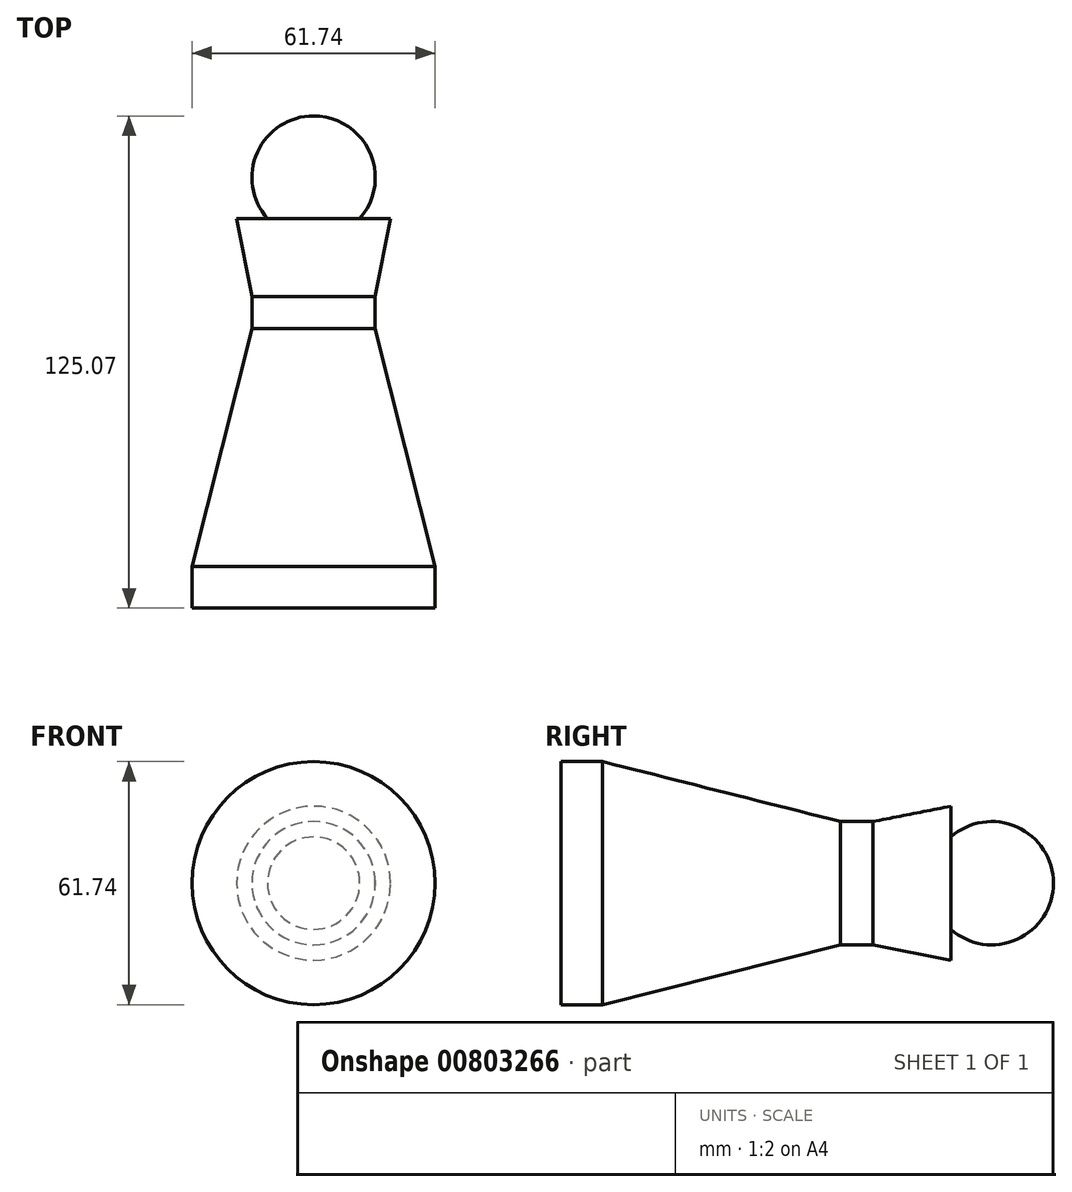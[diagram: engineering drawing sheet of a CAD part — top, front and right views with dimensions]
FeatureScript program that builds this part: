
annotation { "Feature Type Name" : "Feature", "Feature Type Description" : "" }
export const myFeature = defineFeature(function(context is Context, id is Id, definition is map)
    precondition{}
    {
        {
            var Q0;
            Q0=qCreatedBy(makeId("Top.planeOp"),FACE);
            var sketch = newSketch(context, id + "F0", { "sketchPlane" : qUnion([Q0])});
            skLineSegment(sketch, "E0", {"start": v(0, 76.2) * mm, "end": v(0, -62.86) * mm, "construction": true});
            skLineSegment(sketch, "E1.top", {"start": v(0, -55.81) * mm, "end": v(30.87, -55.81) * mm});
            skLineSegment(sketch, "E1.left", {"start": v(0, -45.24) * mm, "end": v(0, -55.81) * mm});
            skLineSegment(sketch, "E1.right", {"start": v(30.87, -45.24) * mm, "end": v(30.87, -55.81) * mm});
            skLineSegment(sketch, "E2.right", {"start": v(15.67, 23.36) * mm, "end": v(15.67, 15.2) * mm});
            skLineSegment(sketch, "E3", {"start": v(15.67, 15.2) * mm, "end": v(30.87, -45.24) * mm});
            skArc(sketch, "E4", {"start": v(11.74, 43.2) * mm, "mid": v(14.29, 60.03) * mm, "end": v(0, 69.26) * mm});
            skLineSegment(sketch, "E5", {"start": v(11.74, 43.2) * mm, "end": v(19.56, 43.2) * mm});
            skLineSegment(sketch, "E6", {"start": v(19.56, 43.2) * mm, "end": v(15.67, 23.36) * mm});
            skLineSegment(sketch, "E7", {"start": v(0, 69.26) * mm, "end": v(0, -55.81) * mm});
            skSolve(sketch);
        }
        {
            var Q0;
            {var subQ0=sQuery(id+"F0.wireOp",EDGE,"E1.top");Q0=makeQuery(id+"F0.imprint","IMPRINT",FACE,{"disambiguationData":[TD([[makeQuery(id+"F0.imprint","IMPRINT",EDGE,{"derivedFrom":subQ0}),1.0]])]});}
            var Q1;
            Q1=sQuery(id+"F0.wireOp",EDGE,"E0");
            revolve(context, id + "F1", {"surfaceOperationType" : NewSurfaceOperationType.NEW, "entities" : qUnion([Q0]), "axis" : qUnion([Q1]), "revolveType" : RevolveType.FULL});
        }
    });
